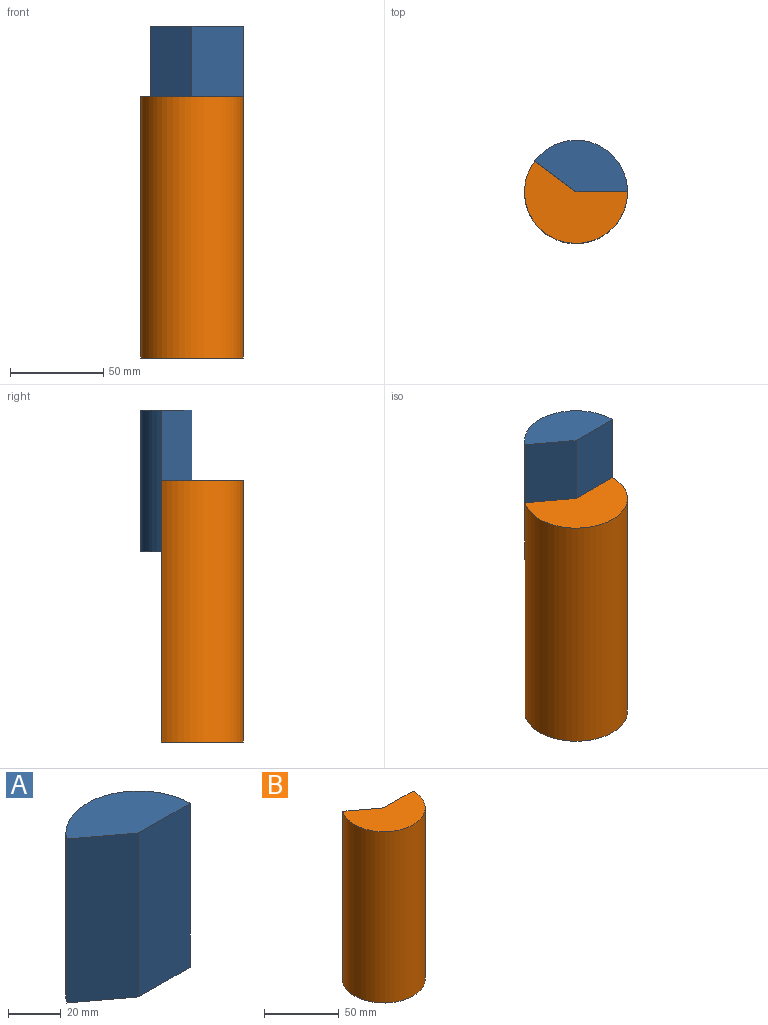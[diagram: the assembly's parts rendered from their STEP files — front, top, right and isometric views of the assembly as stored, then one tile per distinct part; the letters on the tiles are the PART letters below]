
ASSEMBLY  parts=2 mates=1
PART A: 5 faces, bbox 49.8x27.6x76.2 mm
  f0: plane 76.2x27.64mm, normal (0,-1,0), area 2105.9mm2, adj f1,f2,f3,f4
  f1: cylinder r=27.64mm len=76.2mm, axis (0,0,-1), area 5268.2mm2, adj f0,f2,f3,f4
  f2: plane 76.2x22.17mm, normal (-0.6,-0.8,0), area 2105.9mm2, adj f0,f1,f3,f4
  f3: plane 49.8x27.64mm, normal (0,0,1), area 955.4mm2, adj f0,f1,f2
  f4: plane 49.8x27.64mm, normal (0,0,-1), area 955.4mm2, adj f0,f1,f2
PART B: 5 faces, bbox 55.3x44.1x140.1 mm
  f0: cylinder r=27.64mm len=140.15mm, axis (0,0,-1), area 14646.9mm2, adj f1,f2,f3,f4
  f1: plane 140.15x27.64mm, normal (0,1,0), area 3873.2mm2, adj f0,f2,f3,f4
  f2: plane 140.15x22.17mm, normal (0.6,0.8,0), area 3873.2mm2, adj f0,f1,f3,f4
  f3: plane 55.27x44.14mm, normal (0,0,1), area 1444.2mm2, adj f0,f1,f2
  f4: plane 55.27x44.14mm, normal (0,0,-1), area 1444.2mm2, adj f0,f1,f2
PLACE A t=(2.29,-71.27,47.84)mm
PLACE B t=(2.29,45.82,-54.21)mm
MATE fastened B.f0 <-> A.f1  axis (0,0,1) through (42.63,15.21,85.94)mm
